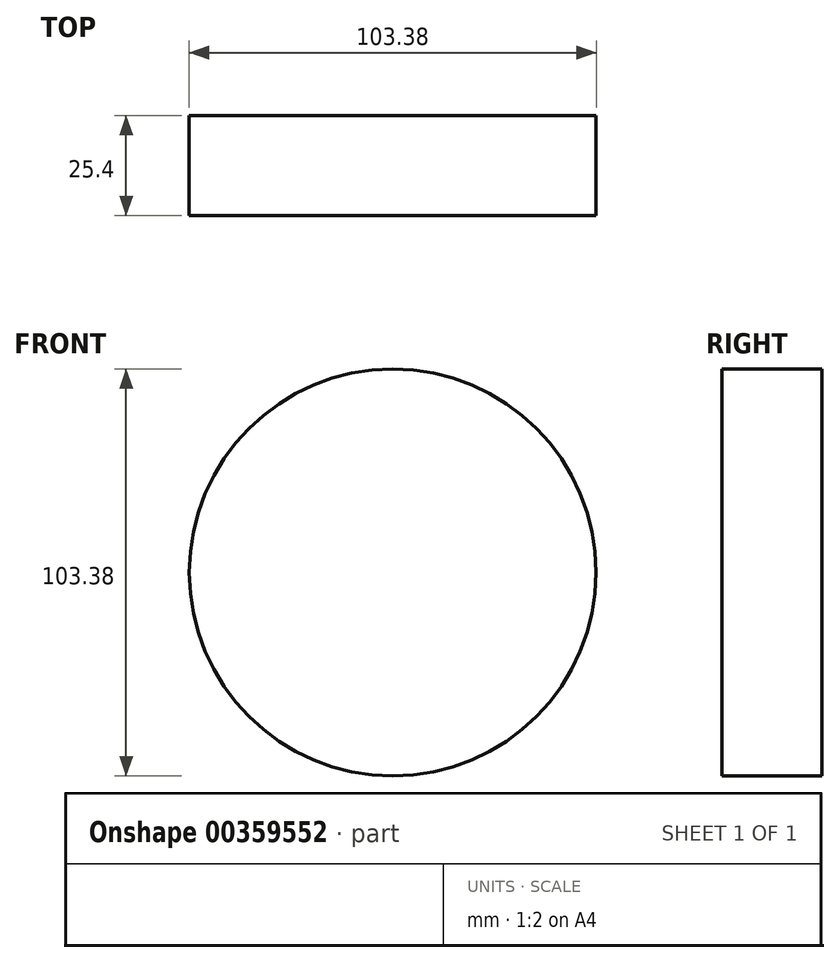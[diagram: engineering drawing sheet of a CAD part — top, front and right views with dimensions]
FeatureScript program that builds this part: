
annotation { "Feature Type Name" : "Feature", "Feature Type Description" : "" }
export const myFeature = defineFeature(function(context is Context, id is Id, definition is map)
    precondition{}
    {
        {
            var Q0;
            Q0=qCreatedBy(makeId("Front.planeOp"),FACE);
            var sketch = newSketch(context, id + "F0", { "sketchPlane" : qUnion([Q0])});
            skCircle(sketch, "E0", {"center": v(0, 0) * mm, "radius": 51.69 * mm});
            skSolve(sketch);
        }
        {
            var Q0;
            Q0=sQuery(id+"F0.wireOp",EDGE,"E0");
            extrude(context, id + "F1", {"bodyType" : ToolBodyType.SURFACE, "surfaceEntities" : qUnion([Q0]), "depth" : 25.4 * mm});
        }
    });
